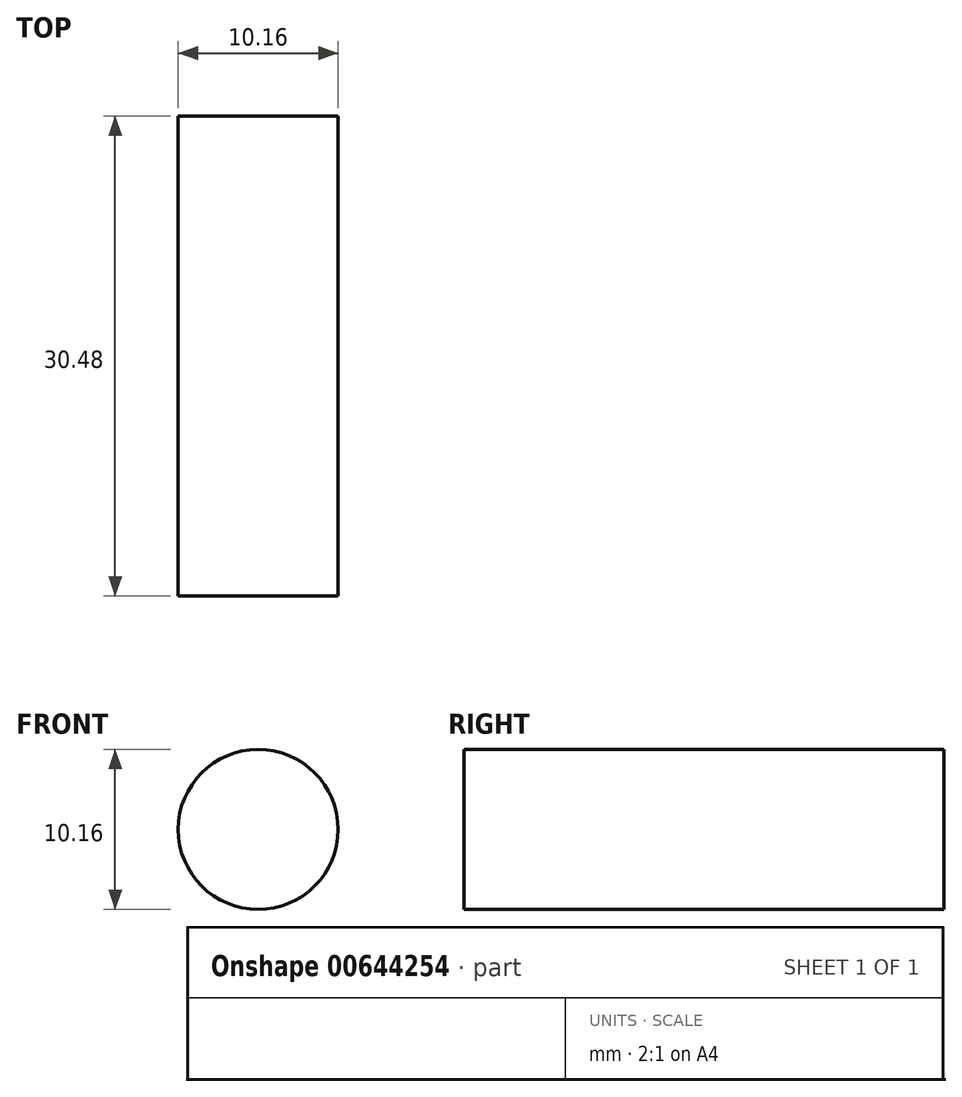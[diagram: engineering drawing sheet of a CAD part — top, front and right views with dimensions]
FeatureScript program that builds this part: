
annotation { "Feature Type Name" : "Feature", "Feature Type Description" : "" }
export const myFeature = defineFeature(function(context is Context, id is Id, definition is map)
    precondition{}
    {
        {
            var Q0;
            Q0=qCreatedBy(makeId("Front.planeOp"),FACE);
            var sketch = newSketch(context, id + "F0", { "sketchPlane" : qUnion([Q0])});
            skCircle(sketch, "E0", {"center": v(0, 0) * mm, "radius": 5.08 * mm});
            skSolve(sketch);
        }
        {
            var Q0;
            Q0 = qSketchRegion(id + "F0", true);
            extrude(context, id + "F1", {"entities" : qUnion([Q0]), "depth" : 30.48 * mm, "offsetDistance" : 25.4 * mm});
        }
    });
